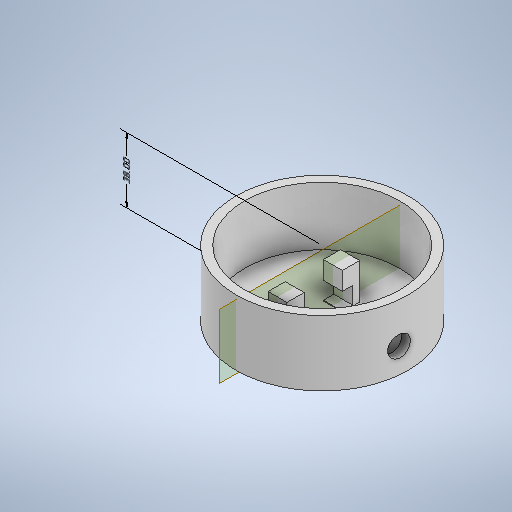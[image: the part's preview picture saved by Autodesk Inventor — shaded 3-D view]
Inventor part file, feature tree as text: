
AUTODESK INVENTOR PART (.ipt)
format: ipt  version: 2025.2 (Build 292293000, 293)  size: 488,448 bytes
history: native  units: mm
features: extrude x5, other x4, sketch x4
ambient origin geometry x8: Origin, YZ Plane, XZ Plane, XY Plane, X Axis, Y Axis, Z Axis, Center Point
bodies: Body1 (feature_tree)
feature tree (13):
  other  "Bryła1"
  other  "Opisy"
  sketch  "Szkic1"
  extrude  "Wyciągnięcie proste1"  Depth=100.0mm
  extrude  "Wyciągnięcie proste2"  Depth=90.0mm
  extrude  "Wyciągnięcie proste3"  Depth=11.0mm
  extrude  "Wyciągnięcie proste4"  Depth=10.0mm
  other  "Płaszczyzna konstrukcyjna1"
  extrude  "Wyciągnięcie proste5"  Depth=11.0mm
  sketch  "Szkic4"
  sketch  "Szkic2"
  sketch  "Szkic3"
  other  "Wymiar liniowy 1"
